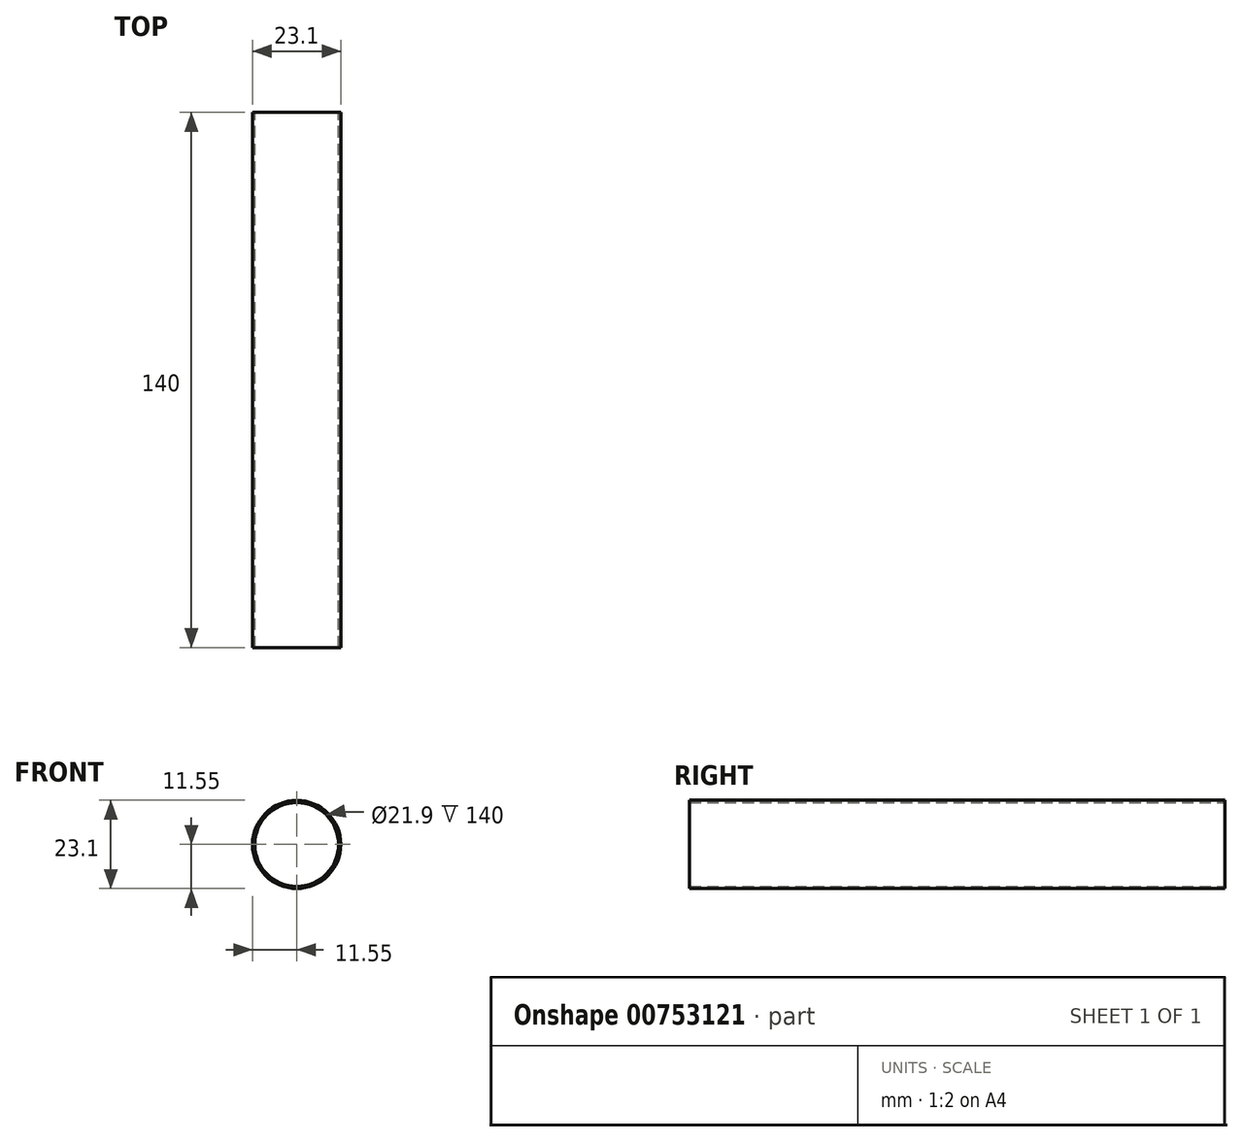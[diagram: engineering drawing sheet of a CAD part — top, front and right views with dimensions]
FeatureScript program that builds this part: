
annotation { "Feature Type Name" : "Feature", "Feature Type Description" : "" }
export const myFeature = defineFeature(function(context is Context, id is Id, definition is map)
    precondition{}
    {
        {
            var Q0;
            Q0=qCreatedBy(makeId("Front.planeOp"),FACE);
            var sketch = newSketch(context, id + "F0", { "sketchPlane" : qUnion([Q0])});
            skCircle(sketch, "E0", {"center": v(0, 0) * mm, "radius": 10.95 * mm});
            skCircle(sketch, "E1.0", {"center": v(0, 0) * mm, "radius": 11.55 * mm});
            skSolve(sketch);
        }
        {
            var Q0;
            Q0 = qSketchRegion(id + "F0", true);
            extrude(context, id + "F1", {"entities" : qUnion([Q0]), "depth" : 140 * mm, "offsetDistance" : 25 * mm});
        }
    });
